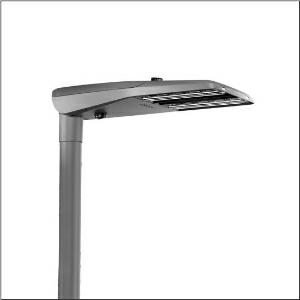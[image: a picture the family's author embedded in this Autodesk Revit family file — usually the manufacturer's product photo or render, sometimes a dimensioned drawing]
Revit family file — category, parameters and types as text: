
# Revit family: streetlight_sl_11_iq_midi___pc-r_5xc3f21y08me_3682
name_source: partatom
category: Lighting Fixtures
units: mm (PartAtom-declared; Revit-internal decimal feet)

## family parameters
Cut with Voids When Loaded = No
Host = Face
Light Source = No
Part Type = Normal
Room Calculation Point = No
Round Connector Dimension = Use Diameter
Shared = No

## types (1)
- --- (1 x LED, 12730 lm, 122.8 W, 2200K)
    Apparent Load = 123 VA
    CIE Flux Codes = 37 73 96 100 100
    Color Rendering = 70
    Color Temperature = 2200K
    Default Elevation = 1800 mm
    Description = Streetlight SL 11 iQ midi, mast luminaire, primary light control with 3 zone facetted reflector, of plastic, silver coated, highly specular, primary optical cover: cover, of PMMA, transparent, light distribution: PC-R, light emission: direct distribution, primary light characteristic: asymmetric, right, installation type: post-top, side-entry, lamps: LED, High Power LED, rated values: 12.730lm | 122,8W | 103,7lm/W (begin service life); end service life: 12.730lm | 130,2W; at 50% lumin. flux: 6.365lm | 56W | 113,7lm/W, colour temperature: 2200K, colour rendering: CRI > 70, light colour: 722, light setting 1 begin service life: 100% | 12.730lm | 122,8W | 103,7lm/W | 2.200K, light setting 1 end service life: 130,2W, further light settings possible, control: pre-setting: logarithmic dimming characteristic, Street-Remote, Auto-Match, Temp-Guard, Lumen-Switch, Night-Set, Smart-Wire, Light-Fading, Desk-Remote (wireless, voltage-free reading and setting of iQ features in the workshop via application-optimized NFC function/RFID function), optimised constant luminous flux control (CLO 2.0), with cable H07RN-F 5x 1.5mm², mains connection: 230..240V, AC, 50/60Hz, connection cable pre-assembled, cable length: 12,5m, luminaire housing, of diecast aluminium, powder-coated, Siteco® metallic grey (DB 702S), please order mast flange separately, inclination adjustable without tools: 0°, 5°, 10°, 15° (post-top) | 0°, -5°, -10°, -15° (side-entry), sealing non-destructively replaceable, multi-level sealing system, length: 780mm, width: 376mm, height: 118mm, mast flange for spigot size: 42mm (side-entry): 5XC10008XM4, 60/48mm (side-entry/post-top): 5XC10108XM2, 76/60mm (side-entry/post-top): 5XC10108XM1, equipment: Power, Smart Interface below and above, protection rating (complete): IP66, insulation class (complete): insulation class II (safety insulation), certification: CE, ENEC, ENEC+, VDE, UKCA, impact resistance: IK10, permissible operating ambient temperature for outdoor applications: -25..+50°C, standard-compliant lighting for roads and squares, Environmental Product Declaration (EPD) tested and certified by an independent institute, packaging unit: 1 piece

Light Distribution: PC-R
    Height = 118 mm
    Lamp = 1 x LED
    Lamp Light Flux = 12730 lm
    Lamp Power = 122.8 W
    Lamp count = 1
    Length = 780 mm
    Luminous efficacy = 104 lm/W
    Manufacturer = Siteco
    ModVariant = No
    Model = 5XC3F21Y08ME
    Number of Poles = 1
    OnlyDefault = Yes
    Power Factor = 1
    Product Name = Streetlight SL 11 iQ midi | PC-R
    Product group = mast luminaire | pylon top
    ProductGroupID = 6100
    Protection Class = Protection class II
    Protection Degree = IP 66
    RLX_Detail_Level = 1
    RLX_Emergency_Light_Flux = 0 lm
    RLX_Emergency_Type = 0
    RLX_Emergency_Type_DB = No
    RlxData = <blob elided: 73605 chars, md5=328bb9e4>
    Socket = socket
    Standby Power = 0 W
    System Light Flux = 12729 lm
    System Power = 123 W
    Type Comments = factory setting: luminous flux: 100 % | dim-lin: 254 | 553 mA
    Type Image = l_1004429.jpg
    URL = http://relux.com
    VarID = @adj_126574
    Voltage = 0 V
    Weight = 0.00 kg
    Width = 376 mm

## geometry (parser evidence)
native form markers: Blend x4, Sweep x9
no freeform markers — native parametric forms only
